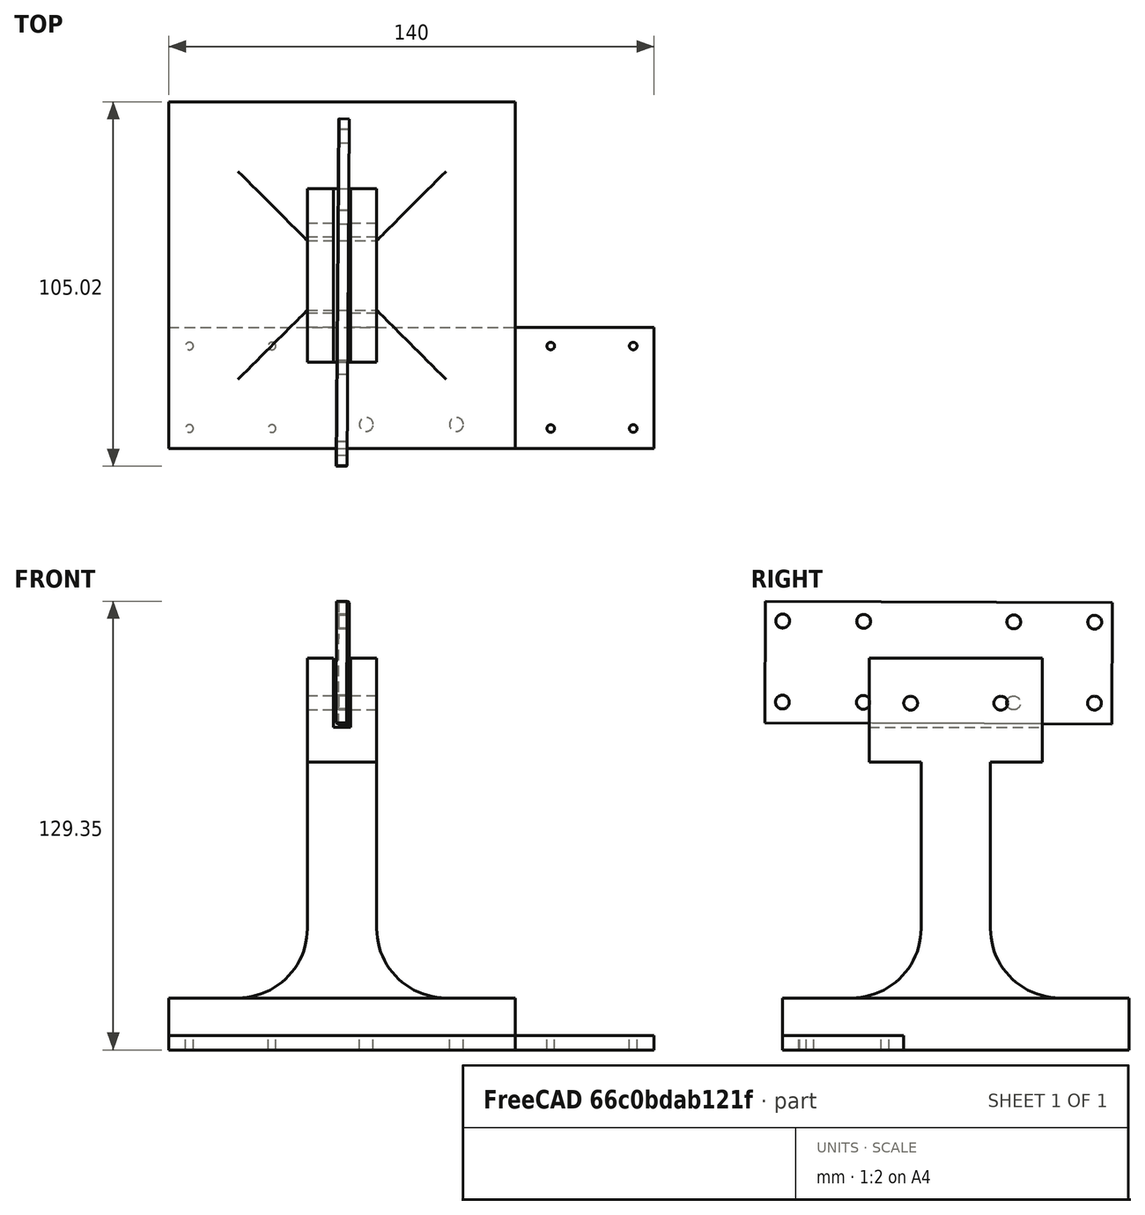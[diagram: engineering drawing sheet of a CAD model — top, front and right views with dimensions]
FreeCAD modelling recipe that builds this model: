
FCSTD DOCUMENT  (FreeCAD 0.16RUnknown)
Label: suporte_v1
License: All rights reserved
LicenseURL: http://en.wikipedia.org/wiki/All_rights_reserved
objects: Part::Cylinder×20, Part::Cut×14, Part::MultiFuse×9, Part::Box×6, PartDesign::Fillet×1
note: 50 computed .brp shape members not serialized (recipe doc carries the construction recipe); baked Part::Feature solids carry a one-line shape summary decoded from their .brp

FEATURE [Part::Box] Box  label="Base"
  Height = 15
  Length = 100
  Width = 100
FEATURE [Part::Box] Box001  label="TroncoSolido"
  Height = 100
  Length = 20
  Placement = pos=(40,40,13) rot=(0,0,1;0rad)
  Width = 20
FEATURE [Part::Box] Box002  label="ChanfroTronco"
  Height = 30
  Length = 5
  Placement = pos=(47.5,25,93) rot=(0,0,1;0rad)
  Width = 50
FEATURE [Part::Cylinder] Cylinder
  Angle = 360
  Height = 10
  Radius = 2
FEATURE [Part::Cylinder] Cylinder001
  Angle = 360
  Height = 10
  Placement = pos=(23.35,0,0) rot=(0,0,1;0rad)
  Radius = 2
FEATURE [Part::Cylinder] Cylinder002
  Angle = 360
  Height = 10
  Placement = pos=(0,23.35,0) rot=(0,0,1;0rad)
  Radius = 2
FEATURE [Part::Cylinder] Cylinder003
  Angle = 360
  Height = 10
  Placement = pos=(23.35,23.35,0) rot=(0,0,1;0rad)
  Radius = 2
FEATURE [Part::Box] Box004  label="Cube"
  Height = 3
  Length = 100
  Placement = pos=(-5,-6,0) rot=(0,0,1;0rad)
  Width = 35
FEATURE [Part::Cut] Cut001
  Base = -> Box004
  Tool = -> Cylinder
FEATURE [Part::Cut] Cut002
  Base = -> Cut001
  Tool = -> Cylinder003
FEATURE [Part::Cut] Cut003
  Base = -> Cut002
  Tool = -> Cylinder001
FEATURE [Part::Cut] Cut004
  Base = -> Cut003
  Tool = -> Cylinder002
FEATURE [Part::Cylinder] Cylinder004
  Angle = 360
  Height = 10
  Placement = pos=(90,23.35,0) rot=(0,0,1;0rad)
  Radius = 2
FEATURE [Part::Cylinder] Cylinder005
  Angle = 360
  Height = 10
  Placement = pos=(90,0,0) rot=(0,0,1;0rad)
  Radius = 2
FEATURE [Part::Cylinder] Cylinder006
  Angle = 360
  Height = 10
  Placement = pos=(66.65,23.35,0) rot=(0,0,1;0rad)
  Radius = 2
FEATURE [Part::Cylinder] Cylinder007
  Angle = 360
  Height = 10
  Placement = pos=(66.65,0,0) rot=(0,0,1;0rad)
  Radius = 2
FEATURE [Part::Cut] Cut005
  Base = -> Cut004
  Tool = -> Cylinder004
FEATURE [Part::Cut] Cut006
  Base = -> Cut005
  Tool = -> Cylinder007
FEATURE [Part::Cut] Cut007
  Base = -> Cut006
  Tool = -> Cylinder006
FEATURE [Part::Cut] Cut008  label="Suporte_SemFurosCentrais"
  Base = -> Cut007
  Placement = pos=(52,90,100) rot=(-0.573216,0.579406,0.579406;4.18879rad)
  Tool = -> Cylinder005
FEATURE [Part::Box] Box005  label="T"
  Height = 30
  Length = 20
  Placement = pos=(40,25,83) rot=(0,0,1;0rad)
  Width = 50
FEATURE [Part::MultiFuse] Fusion  label="TroncoT"
  Shapes = -> [Box005,Box001]
FEATURE [Part::Cut] Cut  label="TroncoChanfro"
  Base = -> Fusion
  Tool = -> Box002
FEATURE [Part::Cylinder] Cylinder009  label="ParafusoTDir"
  Angle = 360
  Height = 25
  Placement = pos=(62.5,37,100) rot=(0,-1,0;1.5708rad)
  Radius = 2
FEATURE [Part::Cylinder] Cylinder010  label="ParafusoTEsq"
  Angle = 360
  Height = 25
  Placement = pos=(62.5,63,100) rot=(0,-1,0;1.5708rad)
  Radius = 2
FEATURE [Part::Cut] Cut009
  Base = -> Cut
  Tool = -> Cylinder009
FEATURE [Part::Cut] Cut010  label="TroncoTParafusos"
  Base = -> Cut009
  Tool = -> Cylinder010
FEATURE [Part::MultiFuse] Fusion001  label="Suporte_v0"
  Shapes = -> [Cut010,Box]
FEATURE [Part::Box] Box006  label="Cube001"
  Height = 4.2
  Length = 140
  Width = 35
FEATURE [Part::Cylinder] Cylinder011  label="FuroSupEsq"
  Angle = 360
  Height = 10
  Radius = 2
FEATURE [Part::Cylinder] Cylinder012  label="FuroSupDir"
  Angle = 360
  Height = 10
  Placement = pos=(26,0,0) rot=(0,0,1;0rad)
  Radius = 2
FEATURE [Part::MultiFuse] Fusion002  label="FurosSup"
  Placement = pos=(57,7,0) rot=(0,0,1;0rad)
  Shapes = -> [Cylinder011,Cylinder012]
FEATURE [Part::Cut] Cut011  label="ChapaComFurosSup"
  Base = -> Box006
  Tool = -> Fusion002
FEATURE [Part::Cylinder] Cylinder013  label="SupEsq"
  Angle = 360
  Height = 10
  Placement = pos=(0,23.8,0) rot=(0,0,1;0rad)
  Radius = 1.1
FEATURE [Part::Cylinder] Cylinder014  label="SupDir"
  Angle = 360
  Height = 10
  Placement = pos=(23.8,23.8,0) rot=(0,0,1;0rad)
  Radius = 1.1
FEATURE [Part::Cylinder] Cylinder015  label="InfEsq"
  Angle = 360
  Height = 10
  Radius = 1.1
FEATURE [Part::Cylinder] Cylinder016  label="InfDir"
  Angle = 360
  Height = 10
  Placement = pos=(23.8,0,0) rot=(0,0,1;0rad)
  Radius = 1.1
FEATURE [Part::MultiFuse] Fusion003
  Shapes = -> [Cylinder013,Cylinder014]
FEATURE [Part::MultiFuse] Fusion004
  Shapes = -> [Fusion003,Cylinder016]
FEATURE [Part::MultiFuse] Fusion005  label="FurosCameraEsq"
  Placement = pos=(6,5.825,0) rot=(0,0,1;0rad)
  Shapes = -> [Fusion004,Cylinder015]
FEATURE [Part::Cylinder] Cylinder017  label="SupEsq001"
  Angle = 360
  Height = 10
  Placement = pos=(0,23.8,0) rot=(0,0,1;0rad)
  Radius = 1.1
FEATURE [Part::Cylinder] Cylinder018  label="SupDir001"
  Angle = 360
  Height = 10
  Placement = pos=(23.8,23.8,0) rot=(0,0,1;0rad)
  Radius = 1.1
FEATURE [Part::Cylinder] Cylinder019  label="InfEsq001"
  Angle = 360
  Height = 10
  Radius = 1.1
FEATURE [Part::Cylinder] Cylinder020  label="InfDir001"
  Angle = 360
  Height = 10
  Placement = pos=(23.8,0,0) rot=(0,0,1;0rad)
  Radius = 1.1
FEATURE [Part::MultiFuse] Fusion006
  Shapes = -> [Cylinder017,Cylinder018]
FEATURE [Part::MultiFuse] Fusion007
  Shapes = -> [Fusion006,Cylinder020]
FEATURE [Part::MultiFuse] Fusion008  label="FurosCameraDir"
  Placement = pos=(110.2,5.825,0) rot=(0,0,1;0rad)
  Shapes = -> [Fusion007,Cylinder019]
FEATURE [Part::Cut] Cut012
  Base = -> Cut011
  Tool = -> Fusion005
FEATURE [Part::Cut] Cut013  label="ChapaCamera"
  Base = -> Cut012
  Tool = -> Fusion008
FEATURE [PartDesign::Fillet] Fillet
  Base = -> Fusion001 [Edge11,Edge10,Edge12,Edge13]
  Radius = 20
